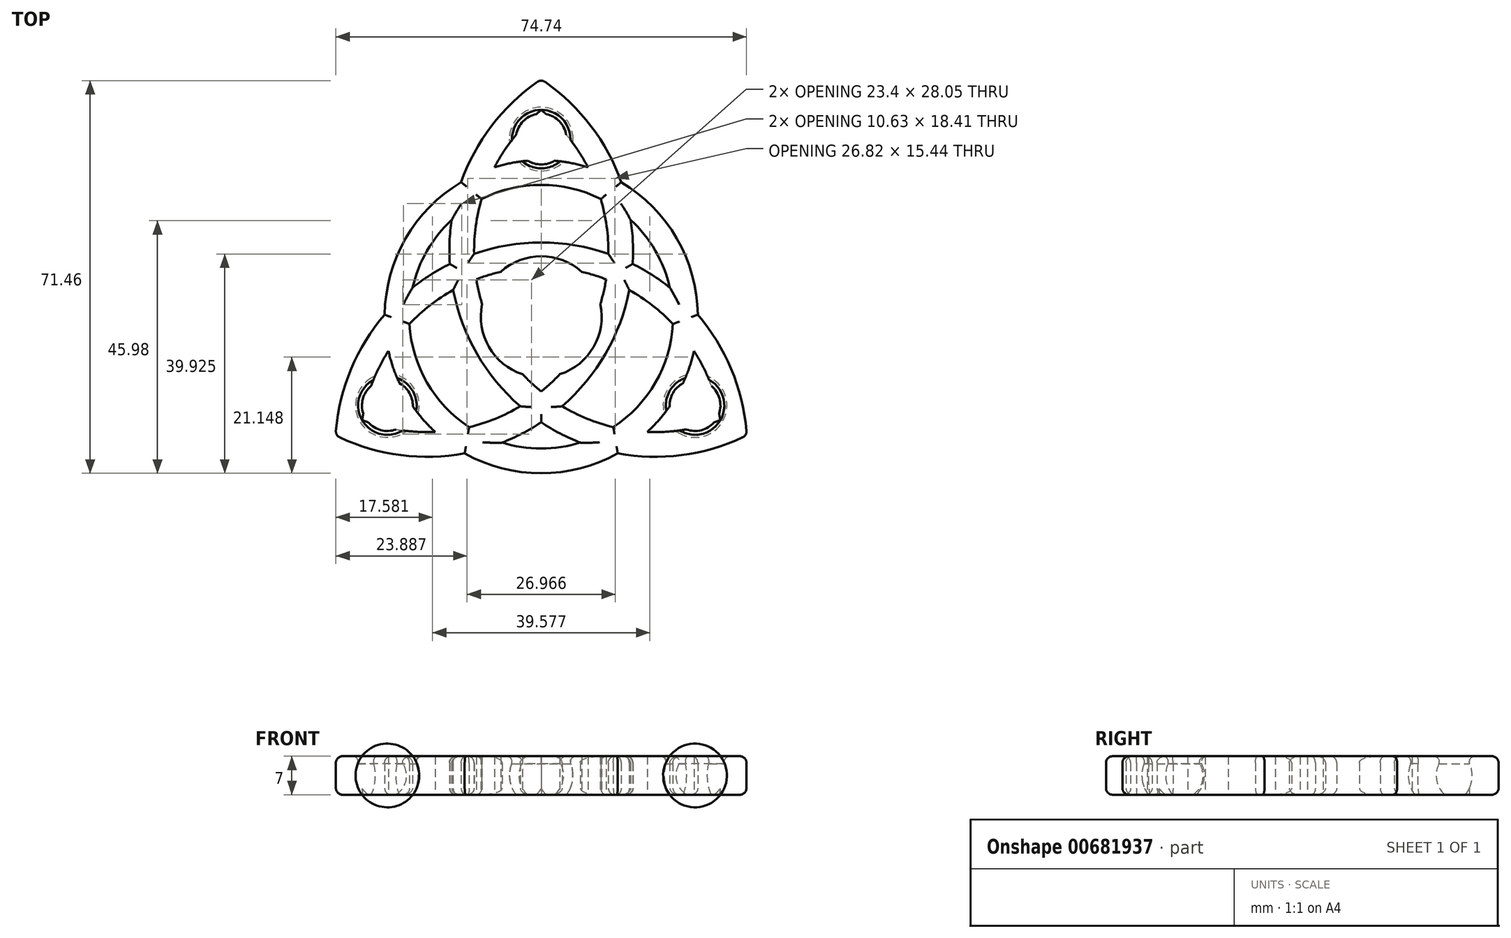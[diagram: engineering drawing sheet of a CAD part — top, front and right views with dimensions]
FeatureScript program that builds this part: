
annotation { "Feature Type Name" : "Feature", "Feature Type Description" : "" }
export const myFeature = defineFeature(function(context is Context, id is Id, definition is map)
    precondition{}
    {
        {
            var Q0;
            Q0=qCreatedBy(makeId("Top.planeOp"),FACE);
            var sketch = newSketch(context, id + "F0", { "sketchPlane" : qUnion([Q0])});
            skLineSegment(sketch, "E0", {"start": v(0, 58.7) * mm, "end": v(0, -66.3) * mm, "construction": true});
            skLineSegment(sketch, "E1", {"start": v(-51.5, -29.73) * mm, "end": v(60.42, 34.88) * mm, "construction": true});
            skLineSegment(sketch, "E2", {"start": v(-60.42, 34.88) * mm, "end": v(51.67, -29.83) * mm, "construction": true});
            skLineSegment(sketch, "E3", {"start": v(-73.13, 34.88) * mm, "end": v(66.87, 34.88) * mm, "construction": true});
            skArc(sketch, "E4", {"start": v(-14.57, 24.5) * mm, "mid": v(-28.35, 2.95) * mm, "end": v(-19.3, -20.97) * mm});
            skArc(sketch, "E5", {"start": v(-16.3, 17.62) * mm, "mid": v(-23.92, -2.01) * mm, "end": v(-13.12, -20.1) * mm});
            skPoint(sketch, "E6", {"position": v(20.78, 12) * mm});
            skArc(sketch, "E7", {"start": v(0, 43.21) * mm, "mid": v(-12.82, 28.64) * mm, "end": v(-16.64, 9.6) * mm});
            skArc(sketch, "E8", {"start": v(0, 37.63) * mm, "mid": v(-9.12, 25.95) * mm, "end": v(-12.21, 11.46) * mm});
            skPoint(sketch, "E9", {"position": v(0, -24) * mm});
            skPoint(sketch, "E10", {"position": v(-20.78, 12) * mm});
            skArc(sketch, "E11", {"start": v(37.42, -21.6) * mm, "mid": v(31.21, -3.22) * mm, "end": v(16.64, 9.6) * mm});
            skArc(sketch, "E12", {"start": v(32.6, -18.82) * mm, "mid": v(27.03, -5.08) * mm, "end": v(16.03, 4.85) * mm});
            skArc(sketch, "E13", {"start": v(-37.42, -21.6) * mm, "mid": v(-18.4, -25.42) * mm, "end": v(0, -19.21) * mm});
            skArc(sketch, "E14", {"start": v(-32.6, -18.82) * mm, "mid": v(-17.91, -20.87) * mm, "end": v(-3.82, -16.3) * mm});
            skArc(sketch, "E15.trimOffspring", {"start": v(8.5, 27.2) * mm, "mid": v(4.8, 32.85) * mm, "end": v(0, 37.63) * mm});
            skArc(sketch, "E16.trimOffspring", {"start": v(14.57, 24.5) * mm, "mid": v(8.8, 35.04) * mm, "end": v(0, 43.21) * mm});
            skArc(sketch, "E17.trimOffspring", {"start": v(12.21, 11.46) * mm, "mid": v(-6.39, 12.95) * mm, "end": v(-23.4, 5.3) * mm});
            skArc(sketch, "E18.trimOffspring", {"start": v(11.8, 6.82) * mm, "mid": v(-7.31, 8.18) * mm, "end": v(-23.96, -1.31) * mm});
            skArc(sketch, "E19.trimOffspring", {"start": v(-11.8, 6.82) * mm, "mid": v(-3.43, -10.42) * mm, "end": v(13.12, -20.1) * mm});
            skArc(sketch, "E20.trimOffspring", {"start": v(-16.03, 4.85) * mm, "mid": v(-8.02, -12) * mm, "end": v(7.12, -22.92) * mm});
            skArc(sketch, "E21.trimOffspring", {"start": v(-7.12, -22.92) * mm, "mid": v(13.7, -19.7) * mm, "end": v(23.96, -1.31) * mm});
            skArc(sketch, "E22.trimOffspring", {"start": v(-13.92, -24.87) * mm, "mid": v(11.62, -26.02) * mm, "end": v(27.8, -6.23) * mm});
            skArc(sketch, "E23.trimOffspring", {"start": v(-27.8, -6.23) * mm, "mid": v(-30.85, -12.28) * mm, "end": v(-32.6, -18.82) * mm});
            skArc(sketch, "E24.trimOffspring", {"start": v(-28.5, 0.37) * mm, "mid": v(-34.74, -9.9) * mm, "end": v(-37.42, -21.6) * mm});
            skArc(sketch, "E25.trimOffspring", {"start": v(13.92, -24.87) * mm, "mid": v(25.94, -25.14) * mm, "end": v(37.42, -21.6) * mm});
            skArc(sketch, "E26.trimOffspring", {"start": v(19.3, -20.97) * mm, "mid": v(26.06, -20.58) * mm, "end": v(32.6, -18.82) * mm});
            skArc(sketch, "E27.trimOffspring", {"start": v(28.5, 0.37) * mm, "mid": v(16.73, 23.07) * mm, "end": v(-8.5, 27.2) * mm});
            skArc(sketch, "E28.trimOffspring", {"start": v(23.4, 5.3) * mm, "mid": v(10.22, 21.72) * mm, "end": v(-10.85, 21.4) * mm});
            skArc(sketch, "E29.trimOffspring", {"start": v(3.82, -16.3) * mm, "mid": v(14.41, -0.94) * mm, "end": v(16.3, 17.62) * mm});
            skArc(sketch, "E30.trimOffspring", {"start": v(0, -13.63) * mm, "mid": v(10.74, 2.24) * mm, "end": v(10.85, 21.4) * mm});
            skSolve(sketch);
        }
        {
            var Q0;
            {var subQ0=sQuery(id+"F0.wireOp",EDGE,"E15.trimOffspring");Q0=makeQuery(id+"F0.imprint","IMPRINT",FACE,{"disambiguationData":[TD([[makeQuery(id+"F0.imprint","IMPRINT",EDGE,{"derivedFrom":subQ0}),-1.0]])]});}
            var Q1;
            {var subQ0=sQuery(id+"F0.wireOp",EDGE,"E27.trimOffspring");var subQ7=sQuery(id+"F0.wireOp",EDGE,"E8");var subQ8=makeQuery(id+"F0.imprint","INTERSECT",VERTEX,{"derivedFrom":[subQ7,subQ0]});Q1=makeQuery(id+"F0.imprint","IMPRINT",FACE,{"disambiguationData":[TD([[makeQuery(id+"F0.imprint","IMPRINT",EDGE,{"disambiguationData":[TD([[subQ8,-1.0]])],"derivedFrom":subQ7}),1.0]])]});}
            var Q2;
            {var subQ0=sQuery(id+"F0.wireOp",EDGE,"E29.trimOffspring");var subQ3=sQuery(id+"F0.wireOp",EDGE,"E19.trimOffspring");var subQ4=makeQuery(id+"F0.imprint","INTERSECT",VERTEX,{"derivedFrom":[subQ3,subQ0]});Q2=makeQuery(id+"F0.imprint","IMPRINT",FACE,{"disambiguationData":[TD([[makeQuery(id+"F0.imprint","IMPRINT",EDGE,{"disambiguationData":[TD([[subQ4,1.0]])],"derivedFrom":subQ3}),1.0]])]});}
            var Q3;
            {var subQ0=sQuery(id+"F0.wireOp",EDGE,"E7");var subQ5=sQuery(id+"F0.wireOp",EDGE,"E4");var subQ9=makeQuery(id+"F0.imprint","INTERSECT",VERTEX,{"derivedFrom":[subQ5,subQ0]});Q3=makeQuery(id+"F0.imprint","IMPRINT",FACE,{"disambiguationData":[TD([[makeQuery(id+"F0.imprint","IMPRINT",EDGE,{"disambiguationData":[TD([[subQ9,-1.0]])],"derivedFrom":subQ5}),1.0]])]});}
            var Q4;
            {var subQ6=sQuery(id+"F0.wireOp",EDGE,"E23.trimOffspring");Q4=makeQuery(id+"F0.imprint","IMPRINT",FACE,{"disambiguationData":[TD([[makeQuery(id+"F0.imprint","IMPRINT",EDGE,{"derivedFrom":subQ6}),-1.0]])]});}
            var Q5;
            {var subQ0=sQuery(id+"F0.wireOp",EDGE,"E21.trimOffspring");var subQ4=sQuery(id+"F0.wireOp",EDGE,"E12");var subQ5=makeQuery(id+"F0.imprint","INTERSECT",VERTEX,{"derivedFrom":[subQ4,subQ0]});Q5=makeQuery(id+"F0.imprint","IMPRINT",FACE,{"disambiguationData":[TD([[makeQuery(id+"F0.imprint","IMPRINT",EDGE,{"disambiguationData":[TD([[subQ5,1.0]])],"derivedFrom":subQ4}),1.0]])]});}
            var Q6;
            {var subQ9=sQuery(id+"F0.wireOp",EDGE,"E25.trimOffspring");Q6=makeQuery(id+"F0.imprint","IMPRINT",FACE,{"disambiguationData":[TD([[makeQuery(id+"F0.imprint","IMPRINT",EDGE,{"derivedFrom":subQ9}),1.0]])]});}
            var Q7;
            {var subQ0=sQuery(id+"F0.wireOp",EDGE,"E17.trimOffspring");var subQ2=sQuery(id+"F0.wireOp",EDGE,"E5");var subQ3=makeQuery(id+"F0.imprint","INTERSECT",VERTEX,{"derivedFrom":[subQ2,subQ0]});Q7=makeQuery(id+"F0.imprint","IMPRINT",FACE,{"disambiguationData":[TD([[makeQuery(id+"F0.imprint","IMPRINT",EDGE,{"disambiguationData":[TD([[subQ3,-1.0]])],"derivedFrom":subQ2}),1.0]])]});}
            var Q8;
            {var subQ1=sQuery(id+"F0.wireOp",EDGE,"E19.trimOffspring");var subQ5=sQuery(id+"F0.wireOp",EDGE,"E18.trimOffspring");var subQ6=makeQuery(id+"F0.imprint","INTERSECT",VERTEX,{"derivedFrom":[subQ5,subQ1]});Q8=makeQuery(id+"F0.imprint","IMPRINT",FACE,{"disambiguationData":[TD([[makeQuery(id+"F0.imprint","IMPRINT",EDGE,{"disambiguationData":[TD([[subQ6,-1.0]])],"derivedFrom":subQ5}),1.0]])]});}
            extrude(context, id + "F1", {"entities" : qUnion([Q0, Q1, Q2, Q3, Q4, Q5, Q6, Q7, Q8]), "depth" : 7 * mm, "offsetDistance" : 25 * mm});
        }
        {
            var Q0;
            Q0=qCreatedBy(makeId("Top.planeOp"),FACE);
            var sketch = newSketch(context, id + "F2", { "sketchPlane" : qUnion([Q0])});
            skCircle(sketch, "E31", {"center": v(0, 0) * mm, "radius": 11 * mm});
            skPoint(sketch, "E32", {"position": v(0, 32.33) * mm});
            skPoint(sketch, "E33.0", {"position": v(0, 37.63) * mm});
            skPoint(sketch, "E34.0", {"position": v(0, 28.5) * mm});
            skPoint(sketch, "E35.0", {"position": v(24.68, -14.25) * mm});
            skPoint(sketch, "E36.0", {"position": v(32.6, -18.82) * mm});
            skPoint(sketch, "E37.0", {"position": v(-32.6, -18.82) * mm});
            skPoint(sketch, "E38.0", {"position": v(-24.68, -14.25) * mm});
            skCircle(sketch, "E39", {"center": v(0, 32.33) * mm, "radius": 5.8 * mm});
            skLineSegment(sketch, "E40", {"start": v(-46.33, -26.75) * mm, "end": v(57.59, 33.25) * mm, "construction": true});
            skLineSegment(sketch, "E41", {"start": v(-57.33, 33.1) * mm, "end": v(46.6, -26.9) * mm, "construction": true});
            skCircle(sketch, "E42.MirrorC", {"center": v(-28, -16.17) * mm, "radius": 5.8 * mm});
            skCircle(sketch, "E43.MirrorC", {"center": v(28, -16.17) * mm, "radius": 5.8 * mm});
            skLineSegment(sketch, "E44", {"start": v(-5.8, 32.33) * mm, "end": v(5.8, 32.33) * mm});
            skLineSegment(sketch, "E45.MirrorCS", {"start": v(-30.9, -11.14) * mm, "end": v(-25.1, -21.19) * mm});
            skLineSegment(sketch, "E46.MirrorCS", {"start": v(25.1, -21.19) * mm, "end": v(30.9, -11.14) * mm});
            skSolve(sketch);
        }
        {
            var Q0;
            Q0=makeQuery(id+"F2.imprint","IMPRINT",FACE,{"disambiguationData":[TD([[makeQuery(id+"F2.imprint","IMPRINT",EDGE,{"derivedFrom":sQuery(id+"F2.wireOp",EDGE,"E31")}),1.0]])]});
            extrude(context, id + "F3", {"entities" : qUnion([Q0]), "operationType" : NewBodyOperationType.REMOVE, "depth" : 7 * mm, "offsetDistance" : 25 * mm});
        }
        {
            var Q0;
            Q0=qCreatedBy(makeId("Top.planeOp"),FACE);
            cPlane(context, id + "F4", {"entities" : qUnion([Q0]), "cplaneType" : CPlaneType.OFFSET, "offset" : 3.5 * mm, "width" : 150 * mm, "height" : 150 * mm});
        }
        {
            var Q0;
            Q0=qCreatedBy(id+"F4.planeOp",FACE);
            var sketch = newSketch(context, id + "F5", { "sketchPlane" : qUnion([Q0])});
            skLineSegment(sketch, "E47.0", {"start": v(-5.8, 32.33) * mm, "end": v(5.8, 32.33) * mm});
            skCircle(sketch, "E48.0", {"center": v(0, 32.33) * mm, "radius": 5.8 * mm});
            skPoint(sketch, "E49.0", {"position": v(28, -16.17) * mm});
            skCircle(sketch, "E50.0", {"center": v(28, -16.17) * mm, "radius": 5.8 * mm});
            skLineSegment(sketch, "E51.0", {"start": v(25.1, -21.19) * mm, "end": v(30.9, -11.14) * mm});
            skCircle(sketch, "E52.0", {"center": v(-28, -16.17) * mm, "radius": 5.8 * mm});
            skLineSegment(sketch, "E53.0", {"start": v(-30.9, -11.14) * mm, "end": v(-25.1, -21.19) * mm});
            skSolve(sketch);
        }
        {
            var Q0;
            {var subQ0=sQuery(id+"F5.wireOp",EDGE,"E47.0");Q0=makeQuery(id+"F5.imprint","IMPRINT",FACE,{"disambiguationData":[TD([[makeQuery(id+"F5.imprint","IMPRINT",EDGE,{"derivedFrom":subQ0}),1.0]])]});}
            var Q1;
            Q1=sQuery(id+"F5.wireOp",EDGE,"E47.0");
            revolve(context, id + "F6", {"operationType" : NewBodyOperationType.REMOVE, "entities" : qUnion([Q0]), "axis" : qUnion([Q1]), "revolveType" : RevolveType.FULL, "oppositeDirection" : true});
        }
        {
            var Q0;
            {var subQ0=sQuery(id+"F5.wireOp",EDGE,"E53.0");Q0=makeQuery(id+"F5.imprint","IMPRINT",FACE,{"disambiguationData":[TD([[makeQuery(id+"F5.imprint","IMPRINT",EDGE,{"derivedFrom":subQ0}),-1.0]])]});}
            var Q1;
            Q1=sQuery(id+"F5.wireOp",EDGE,"E53.0");
            revolve(context, id + "F7", {"operationType" : NewBodyOperationType.REMOVE, "entities" : qUnion([Q0]), "axis" : qUnion([Q1]), "revolveType" : RevolveType.FULL, "oppositeDirection" : true});
        }
        {
            var Q0;
            {var subQ0=sQuery(id+"F5.wireOp",EDGE,"E51.0");Q0=makeQuery(id+"F5.imprint","IMPRINT",FACE,{"disambiguationData":[TD([[makeQuery(id+"F5.imprint","IMPRINT",EDGE,{"derivedFrom":subQ0}),-1.0]])]});}
            var Q1;
            Q1=sQuery(id+"F5.wireOp",EDGE,"E51.0");
            revolve(context, id + "F8", {"operationType" : NewBodyOperationType.REMOVE, "entities" : qUnion([Q0]), "axis" : qUnion([Q1]), "revolveType" : RevolveType.FULL, "oppositeDirection" : true});
        }
        {
            var Q0;
            {var subQ0=sQuery(id+"F0.wireOp",EDGE,"E7");Q0=makeQuery(id+"F1.opExtrude","CAP_EDGE",EDGE,{"disambiguationData":[OSD([subQ0]),TDD([makeQuery(id+"F0.imprint","IMPRINT",EDGE,{"disambiguationData":[TD([[makeQuery(id+"F0.imprint","INTERSECT",VERTEX,{"derivedFrom":[sQuery(id+"F0.wireOp",EDGE,"E4"),subQ0]}),1.0]])],"derivedFrom":subQ0})])],"isStart":false});}
            var Q1;
            Q1=makeQuery(id+"F1.opExtrude","CAP_EDGE",EDGE,{"disambiguationData":[OSD([sQuery(id+"F0.wireOp",EDGE,"E16.trimOffspring")])],"isStart":false});
            var Q2;
            Q2=makeQuery(id+"F1.opExtrude","SWEPT_EDGE",EDGE,{"disambiguationData":[OSD([sQuery(id+"F0.wireOp",EDGE,"E7"),sQuery(id+"F0.wireOp",EDGE,"E16.trimOffspring")])]});
            var Q3;
            {var subQ0=sQuery(id+"F0.wireOp",EDGE,"E4");Q3=makeQuery(id+"F1.opExtrude","CAP_EDGE",EDGE,{"disambiguationData":[OSD([subQ0]),TDD([makeQuery(id+"F0.imprint","IMPRINT",EDGE,{"disambiguationData":[TD([[makeQuery(id+"F0.imprint","INTERSECT",VERTEX,{"derivedFrom":[subQ0,sQuery(id+"F0.wireOp",EDGE,"E7")]}),-1.0]])],"derivedFrom":subQ0})])],"isStart":false});}
            var Q4;
            {var subQ0=sQuery(id+"F0.wireOp",EDGE,"E7");Q4=makeQuery(id+"F1.opExtrude","CAP_EDGE",EDGE,{"disambiguationData":[OSD([subQ0]),TDD([makeQuery(id+"F0.imprint","IMPRINT",EDGE,{"disambiguationData":[TD([[makeQuery(id+"F0.imprint","INTERSECT",VERTEX,{"derivedFrom":[sQuery(id+"F0.wireOp",EDGE,"E5"),subQ0]}),-1.0]])],"derivedFrom":subQ0})])],"isStart":false});}
            var Q5;
            {var subQ0=sQuery(id+"F0.wireOp",EDGE,"E5");Q5=makeQuery(id+"F1.opExtrude","CAP_EDGE",EDGE,{"disambiguationData":[OSD([subQ0]),TDD([makeQuery(id+"F0.imprint","IMPRINT",EDGE,{"disambiguationData":[TD([[makeQuery(id+"F0.imprint","INTERSECT",VERTEX,{"derivedFrom":[subQ0,sQuery(id+"F0.wireOp",EDGE,"E7")]}),-1.0]])],"derivedFrom":subQ0})])],"isStart":false});}
            var Q6;
            {var subQ0=sQuery(id+"F0.wireOp",EDGE,"E17.trimOffspring");Q6=makeQuery(id+"F1.opExtrude","CAP_EDGE",EDGE,{"disambiguationData":[OSD([subQ0]),TDD([makeQuery(id+"F0.imprint","IMPRINT",EDGE,{"disambiguationData":[TD([[makeQuery(id+"F0.imprint","INTERSECT",VERTEX,{"derivedFrom":[sQuery(id+"F0.wireOp",EDGE,"E7"),subQ0]}),-1.0]])],"derivedFrom":subQ0})])],"isStart":false});}
            var Q7;
            {var subQ0=sQuery(id+"F0.wireOp",EDGE,"E17.trimOffspring");Q7=makeQuery(id+"F1.opExtrude","CAP_EDGE",EDGE,{"disambiguationData":[OSD([subQ0]),TDD([makeQuery(id+"F0.imprint","IMPRINT",EDGE,{"disambiguationData":[TD([[makeQuery(id+"F0.imprint","INTERSECT",VERTEX,{"derivedFrom":[sQuery(id+"F0.wireOp",EDGE,"E8"),subQ0]}),1.0]])],"derivedFrom":subQ0})])],"isStart":false});}
            var Q8;
            {var subQ0=sQuery(id+"F0.wireOp",EDGE,"E8");Q8=makeQuery(id+"F1.opExtrude","CAP_EDGE",EDGE,{"disambiguationData":[OSD([subQ0]),TDD([makeQuery(id+"F0.imprint","IMPRINT",EDGE,{"disambiguationData":[TD([[makeQuery(id+"F0.imprint","INTERSECT",VERTEX,{"derivedFrom":[subQ0,sQuery(id+"F0.wireOp",EDGE,"E17.trimOffspring")]}),1.0]])],"derivedFrom":subQ0})])],"isStart":false});}
            var Q9;
            {var subQ0=sQuery(id+"F0.wireOp",EDGE,"E28.trimOffspring");Q9=makeQuery(id+"F1.opExtrude","CAP_EDGE",EDGE,{"disambiguationData":[OSD([subQ0]),TDD([makeQuery(id+"F0.imprint","IMPRINT",EDGE,{"disambiguationData":[TD([[makeQuery(id+"F0.imprint","INTERSECT",VERTEX,{"derivedFrom":[sQuery(id+"F0.wireOp",EDGE,"E8"),subQ0]}),1.0]])],"derivedFrom":subQ0})])],"isStart":false});}
            var Q10;
            {var subQ0=sQuery(id+"F0.wireOp",EDGE,"E30.trimOffspring");Q10=makeQuery(id+"F1.opExtrude","CAP_EDGE",EDGE,{"disambiguationData":[OSD([subQ0]),TDD([makeQuery(id+"F0.imprint","IMPRINT",EDGE,{"disambiguationData":[TD([[makeQuery(id+"F0.imprint","INTERSECT",VERTEX,{"derivedFrom":[sQuery(id+"F0.wireOp",EDGE,"E17.trimOffspring"),subQ0]}),-1.0]])],"derivedFrom":subQ0})])],"isStart":false});}
            var Q11;
            {var subQ0=sQuery(id+"F0.wireOp",EDGE,"E29.trimOffspring");Q11=makeQuery(id+"F1.opExtrude","CAP_EDGE",EDGE,{"disambiguationData":[OSD([subQ0]),TDD([makeQuery(id+"F0.imprint","IMPRINT",EDGE,{"disambiguationData":[TD([[makeQuery(id+"F0.imprint","INTERSECT",VERTEX,{"derivedFrom":[sQuery(id+"F0.wireOp",EDGE,"E11"),subQ0]}),-1.0]])],"derivedFrom":subQ0})])],"isStart":false});}
            var Q12;
            {var subQ0=sQuery(id+"F0.wireOp",EDGE,"E28.trimOffspring");Q12=makeQuery(id+"F1.opExtrude","CAP_EDGE",EDGE,{"disambiguationData":[OSD([subQ0]),TDD([makeQuery(id+"F0.imprint","IMPRINT",EDGE,{"disambiguationData":[TD([[makeQuery(id+"F0.imprint","INTERSECT",VERTEX,{"derivedFrom":[sQuery(id+"F0.wireOp",EDGE,"E11"),subQ0]}),-1.0]])],"derivedFrom":subQ0})])],"isStart":false});}
            var Q13;
            {var subQ0=sQuery(id+"F0.wireOp",EDGE,"E11");Q13=makeQuery(id+"F1.opExtrude","CAP_EDGE",EDGE,{"disambiguationData":[OSD([subQ0]),TDD([makeQuery(id+"F0.imprint","IMPRINT",EDGE,{"disambiguationData":[TD([[makeQuery(id+"F0.imprint","INTERSECT",VERTEX,{"derivedFrom":[subQ0,sQuery(id+"F0.wireOp",EDGE,"E29.trimOffspring")]}),1.0]])],"derivedFrom":subQ0})])],"isStart":false});}
            var Q14;
            {var subQ0=sQuery(id+"F0.wireOp",EDGE,"E27.trimOffspring");Q14=makeQuery(id+"F1.opExtrude","CAP_EDGE",EDGE,{"disambiguationData":[OSD([subQ0]),TDD([makeQuery(id+"F0.imprint","IMPRINT",EDGE,{"disambiguationData":[TD([[makeQuery(id+"F0.imprint","INTERSECT",VERTEX,{"derivedFrom":[sQuery(id+"F0.wireOp",EDGE,"E16.trimOffspring"),subQ0]}),1.0]])],"derivedFrom":subQ0})])],"isStart":false});}
            var Q15;
            {var subQ0=sQuery(id+"F0.wireOp",EDGE,"E11");Q15=makeQuery(id+"F1.opExtrude","CAP_EDGE",EDGE,{"disambiguationData":[OSD([subQ0]),TDD([makeQuery(id+"F0.imprint","IMPRINT",EDGE,{"disambiguationData":[TD([[makeQuery(id+"F0.imprint","INTERSECT",VERTEX,{"derivedFrom":[subQ0,sQuery(id+"F0.wireOp",EDGE,"E25.trimOffspring")]}),-1.0]])],"derivedFrom":subQ0})])],"isStart":false});}
            var Q16;
            {var subQ0=sQuery(id+"F0.wireOp",EDGE,"E21.trimOffspring");Q16=makeQuery(id+"F1.opExtrude","CAP_EDGE",EDGE,{"disambiguationData":[OSD([subQ0]),TDD([makeQuery(id+"F0.imprint","IMPRINT",EDGE,{"disambiguationData":[TD([[makeQuery(id+"F0.imprint","INTERSECT",VERTEX,{"derivedFrom":[sQuery(id+"F0.wireOp",EDGE,"E19.trimOffspring"),subQ0]}),-1.0]])],"derivedFrom":subQ0})])],"isStart":false});}
            var Q17;
            {var subQ0=sQuery(id+"F0.wireOp",EDGE,"E29.trimOffspring");Q17=makeQuery(id+"F1.opExtrude","CAP_EDGE",EDGE,{"disambiguationData":[OSD([subQ0]),TDD([makeQuery(id+"F0.imprint","IMPRINT",EDGE,{"disambiguationData":[TD([[makeQuery(id+"F0.imprint","INTERSECT",VERTEX,{"derivedFrom":[sQuery(id+"F0.wireOp",EDGE,"E12"),subQ0]}),1.0]])],"derivedFrom":subQ0})])],"isStart":false});}
            var Q18;
            {var subQ0=sQuery(id+"F0.wireOp",EDGE,"E20.trimOffspring");Q18=makeQuery(id+"F1.opExtrude","CAP_EDGE",EDGE,{"disambiguationData":[OSD([subQ0]),TDD([makeQuery(id+"F0.imprint","IMPRINT",EDGE,{"disambiguationData":[TD([[makeQuery(id+"F0.imprint","INTERSECT",VERTEX,{"derivedFrom":[sQuery(id+"F0.wireOp",EDGE,"E14"),subQ0]}),1.0]])],"derivedFrom":subQ0})])],"isStart":false});}
            var Q19;
            {var subQ0=sQuery(id+"F0.wireOp",EDGE,"E14");Q19=makeQuery(id+"F1.opExtrude","CAP_EDGE",EDGE,{"disambiguationData":[OSD([subQ0]),TDD([makeQuery(id+"F0.imprint","IMPRINT",EDGE,{"disambiguationData":[TD([[makeQuery(id+"F0.imprint","INTERSECT",VERTEX,{"derivedFrom":[sQuery(id+"F0.wireOp",EDGE,"E5"),subQ0]}),-1.0]])],"derivedFrom":subQ0})])],"isStart":false});}
            var Q20;
            {var subQ0=sQuery(id+"F0.wireOp",EDGE,"E5");Q20=makeQuery(id+"F1.opExtrude","CAP_EDGE",EDGE,{"disambiguationData":[OSD([subQ0]),TDD([makeQuery(id+"F0.imprint","IMPRINT",EDGE,{"disambiguationData":[TD([[makeQuery(id+"F0.imprint","INTERSECT",VERTEX,{"derivedFrom":[subQ0,sQuery(id+"F0.wireOp",EDGE,"E14")]}),1.0]])],"derivedFrom":subQ0})])],"isStart":false});}
            var Q21;
            {var subQ0=sQuery(id+"F0.wireOp",EDGE,"E18.trimOffspring");Q21=makeQuery(id+"F1.opExtrude","CAP_EDGE",EDGE,{"disambiguationData":[OSD([subQ0]),TDD([makeQuery(id+"F0.imprint","IMPRINT",EDGE,{"disambiguationData":[TD([[makeQuery(id+"F0.imprint","INTERSECT",VERTEX,{"derivedFrom":[sQuery(id+"F0.wireOp",EDGE,"E5"),subQ0]}),1.0]])],"derivedFrom":subQ0})])],"isStart":false});}
            var Q22;
            Q22=makeQuery(id+"F1.opExtrude","CAP_EDGE",EDGE,{"disambiguationData":[OSD([sQuery(id+"F0.wireOp",EDGE,"E25.trimOffspring")])],"isStart":false});
            var Q23;
            {var subQ0=sQuery(id+"F0.wireOp",EDGE,"E22.trimOffspring");Q23=makeQuery(id+"F1.opExtrude","CAP_EDGE",EDGE,{"disambiguationData":[OSD([subQ0]),TDD([makeQuery(id+"F0.imprint","IMPRINT",EDGE,{"disambiguationData":[TD([[makeQuery(id+"F0.imprint","INTERSECT",VERTEX,{"derivedFrom":[sQuery(id+"F0.wireOp",EDGE,"E13"),subQ0]}),-1.0]])],"derivedFrom":subQ0})])],"isStart":false});}
            var Q24;
            Q24=makeQuery(id+"F1.opExtrude","SWEPT_EDGE",EDGE,{"disambiguationData":[OSD([sQuery(id+"F0.wireOp",EDGE,"E11"),sQuery(id+"F0.wireOp",EDGE,"E25.trimOffspring")])]});
            var Q25;
            Q25=makeQuery(id+"F1.opExtrude","CAP_EDGE",EDGE,{"disambiguationData":[OSD([sQuery(id+"F0.wireOp",EDGE,"E24.trimOffspring")])],"isStart":false});
            var Q26;
            {var subQ0=sQuery(id+"F0.wireOp",EDGE,"E13");Q26=makeQuery(id+"F1.opExtrude","CAP_EDGE",EDGE,{"disambiguationData":[OSD([subQ0]),TDD([makeQuery(id+"F0.imprint","IMPRINT",EDGE,{"disambiguationData":[TD([[makeQuery(id+"F0.imprint","INTERSECT",VERTEX,{"derivedFrom":[subQ0,sQuery(id+"F0.wireOp",EDGE,"E24.trimOffspring")]}),-1.0]])],"derivedFrom":subQ0})])],"isStart":false});}
            var Q27;
            Q27=makeQuery(id+"F1.opExtrude","SWEPT_EDGE",EDGE,{"disambiguationData":[OSD([sQuery(id+"F0.wireOp",EDGE,"E13"),sQuery(id+"F0.wireOp",EDGE,"E24.trimOffspring")])]});
            var Q28;
            Q28=makeQuery(id+"F1.opExtrude","CAP_EDGE",EDGE,{"disambiguationData":[OSD([sQuery(id+"F0.wireOp",EDGE,"E24.trimOffspring")])],"isStart":true});
            var Q29;
            {var subQ0=sQuery(id+"F0.wireOp",EDGE,"E5");Q29=makeQuery(id+"F1.opExtrude","CAP_EDGE",EDGE,{"disambiguationData":[OSD([subQ0]),TDD([makeQuery(id+"F0.imprint","IMPRINT",EDGE,{"disambiguationData":[TD([[makeQuery(id+"F0.imprint","INTERSECT",VERTEX,{"derivedFrom":[subQ0,sQuery(id+"F0.wireOp",EDGE,"E14")]}),1.0]])],"derivedFrom":subQ0})])],"isStart":true});}
            var Q30;
            {var subQ0=sQuery(id+"F0.wireOp",EDGE,"E18.trimOffspring");Q30=makeQuery(id+"F1.opExtrude","CAP_EDGE",EDGE,{"disambiguationData":[OSD([subQ0]),TDD([makeQuery(id+"F0.imprint","IMPRINT",EDGE,{"disambiguationData":[TD([[makeQuery(id+"F0.imprint","INTERSECT",VERTEX,{"derivedFrom":[sQuery(id+"F0.wireOp",EDGE,"E5"),subQ0]}),1.0]])],"derivedFrom":subQ0})])],"isStart":true});}
            var Q31;
            {var subQ0=sQuery(id+"F0.wireOp",EDGE,"E20.trimOffspring");Q31=makeQuery(id+"F1.opExtrude","CAP_EDGE",EDGE,{"disambiguationData":[OSD([subQ0]),TDD([makeQuery(id+"F0.imprint","IMPRINT",EDGE,{"disambiguationData":[TD([[makeQuery(id+"F0.imprint","INTERSECT",VERTEX,{"derivedFrom":[sQuery(id+"F0.wireOp",EDGE,"E14"),subQ0]}),1.0]])],"derivedFrom":subQ0})])],"isStart":true});}
            var Q32;
            {var subQ0=sQuery(id+"F0.wireOp",EDGE,"E5");Q32=makeQuery(id+"F1.opExtrude","CAP_EDGE",EDGE,{"disambiguationData":[OSD([subQ0]),TDD([makeQuery(id+"F0.imprint","IMPRINT",EDGE,{"disambiguationData":[TD([[makeQuery(id+"F0.imprint","INTERSECT",VERTEX,{"derivedFrom":[subQ0,sQuery(id+"F0.wireOp",EDGE,"E7")]}),-1.0]])],"derivedFrom":subQ0})])],"isStart":true});}
            var Q33;
            {var subQ0=sQuery(id+"F0.wireOp",EDGE,"E17.trimOffspring");Q33=makeQuery(id+"F1.opExtrude","CAP_EDGE",EDGE,{"disambiguationData":[OSD([subQ0]),TDD([makeQuery(id+"F0.imprint","IMPRINT",EDGE,{"disambiguationData":[TD([[makeQuery(id+"F0.imprint","INTERSECT",VERTEX,{"derivedFrom":[sQuery(id+"F0.wireOp",EDGE,"E7"),subQ0]}),-1.0]])],"derivedFrom":subQ0})])],"isStart":true});}
            var Q34;
            {var subQ0=sQuery(id+"F0.wireOp",EDGE,"E4");Q34=makeQuery(id+"F1.opExtrude","CAP_EDGE",EDGE,{"disambiguationData":[OSD([subQ0]),TDD([makeQuery(id+"F0.imprint","IMPRINT",EDGE,{"disambiguationData":[TD([[makeQuery(id+"F0.imprint","INTERSECT",VERTEX,{"derivedFrom":[subQ0,sQuery(id+"F0.wireOp",EDGE,"E7")]}),-1.0]])],"derivedFrom":subQ0})])],"isStart":true});}
            var Q35;
            {var subQ0=sQuery(id+"F0.wireOp",EDGE,"E7");Q35=makeQuery(id+"F1.opExtrude","CAP_EDGE",EDGE,{"disambiguationData":[OSD([subQ0]),TDD([makeQuery(id+"F0.imprint","IMPRINT",EDGE,{"disambiguationData":[TD([[makeQuery(id+"F0.imprint","INTERSECT",VERTEX,{"derivedFrom":[sQuery(id+"F0.wireOp",EDGE,"E4"),subQ0]}),1.0]])],"derivedFrom":subQ0})])],"isStart":true});}
            var Q36;
            {var subQ0=sQuery(id+"F0.wireOp",EDGE,"E7");Q36=makeQuery(id+"F1.opExtrude","CAP_EDGE",EDGE,{"disambiguationData":[OSD([subQ0]),TDD([makeQuery(id+"F0.imprint","IMPRINT",EDGE,{"disambiguationData":[TD([[makeQuery(id+"F0.imprint","INTERSECT",VERTEX,{"derivedFrom":[sQuery(id+"F0.wireOp",EDGE,"E5"),subQ0]}),-1.0]])],"derivedFrom":subQ0})])],"isStart":true});}
            var Q37;
            {var subQ0=sQuery(id+"F0.wireOp",EDGE,"E17.trimOffspring");Q37=makeQuery(id+"F1.opExtrude","CAP_EDGE",EDGE,{"disambiguationData":[OSD([subQ0]),TDD([makeQuery(id+"F0.imprint","IMPRINT",EDGE,{"disambiguationData":[TD([[makeQuery(id+"F0.imprint","INTERSECT",VERTEX,{"derivedFrom":[sQuery(id+"F0.wireOp",EDGE,"E8"),subQ0]}),1.0]])],"derivedFrom":subQ0})])],"isStart":true});}
            var Q38;
            {var subQ0=sQuery(id+"F0.wireOp",EDGE,"E14");Q38=makeQuery(id+"F1.opExtrude","CAP_EDGE",EDGE,{"disambiguationData":[OSD([subQ0]),TDD([makeQuery(id+"F0.imprint","IMPRINT",EDGE,{"disambiguationData":[TD([[makeQuery(id+"F0.imprint","INTERSECT",VERTEX,{"derivedFrom":[sQuery(id+"F0.wireOp",EDGE,"E5"),subQ0]}),-1.0]])],"derivedFrom":subQ0})])],"isStart":true});}
            var Q39;
            {var subQ0=sQuery(id+"F0.wireOp",EDGE,"E13");Q39=makeQuery(id+"F1.opExtrude","CAP_EDGE",EDGE,{"disambiguationData":[OSD([subQ0]),TDD([makeQuery(id+"F0.imprint","IMPRINT",EDGE,{"disambiguationData":[TD([[makeQuery(id+"F0.imprint","INTERSECT",VERTEX,{"derivedFrom":[subQ0,sQuery(id+"F0.wireOp",EDGE,"E20.trimOffspring")]}),1.0]])],"derivedFrom":subQ0})])],"isStart":true});}
            var Q40;
            {var subQ0=sQuery(id+"F0.wireOp",EDGE,"E21.trimOffspring");Q40=makeQuery(id+"F1.opExtrude","CAP_EDGE",EDGE,{"disambiguationData":[OSD([subQ0]),TDD([makeQuery(id+"F0.imprint","IMPRINT",EDGE,{"disambiguationData":[TD([[makeQuery(id+"F0.imprint","INTERSECT",VERTEX,{"derivedFrom":[sQuery(id+"F0.wireOp",EDGE,"E20.trimOffspring"),subQ0]}),1.0]])],"derivedFrom":subQ0})])],"isStart":true});}
            var Q41;
            {var subQ0=sQuery(id+"F0.wireOp",EDGE,"E20.trimOffspring");Q41=makeQuery(id+"F1.opExtrude","CAP_EDGE",EDGE,{"disambiguationData":[OSD([subQ0]),TDD([makeQuery(id+"F0.imprint","IMPRINT",EDGE,{"disambiguationData":[TD([[makeQuery(id+"F0.imprint","INTERSECT",VERTEX,{"derivedFrom":[sQuery(id+"F0.wireOp",EDGE,"E13"),subQ0]}),-1.0]])],"derivedFrom":subQ0})])],"isStart":true});}
            var Q42;
            {var subQ0=sQuery(id+"F0.wireOp",EDGE,"E13");Q42=makeQuery(id+"F1.opExtrude","CAP_EDGE",EDGE,{"disambiguationData":[OSD([subQ0]),TDD([makeQuery(id+"F0.imprint","IMPRINT",EDGE,{"disambiguationData":[TD([[makeQuery(id+"F0.imprint","INTERSECT",VERTEX,{"derivedFrom":[subQ0,sQuery(id+"F0.wireOp",EDGE,"E24.trimOffspring")]}),-1.0]])],"derivedFrom":subQ0})])],"isStart":true});}
            var Q43;
            {var subQ0=sQuery(id+"F0.wireOp",EDGE,"E22.trimOffspring");Q43=makeQuery(id+"F1.opExtrude","CAP_EDGE",EDGE,{"disambiguationData":[OSD([subQ0]),TDD([makeQuery(id+"F0.imprint","IMPRINT",EDGE,{"disambiguationData":[TD([[makeQuery(id+"F0.imprint","INTERSECT",VERTEX,{"derivedFrom":[sQuery(id+"F0.wireOp",EDGE,"E13"),subQ0]}),-1.0]])],"derivedFrom":subQ0})])],"isStart":true});}
            var Q44;
            {var subQ0=sQuery(id+"F0.wireOp",EDGE,"E29.trimOffspring");Q44=makeQuery(id+"F1.opExtrude","CAP_EDGE",EDGE,{"disambiguationData":[OSD([subQ0]),TDD([makeQuery(id+"F0.imprint","IMPRINT",EDGE,{"disambiguationData":[TD([[makeQuery(id+"F0.imprint","INTERSECT",VERTEX,{"derivedFrom":[sQuery(id+"F0.wireOp",EDGE,"E12"),subQ0]}),1.0]])],"derivedFrom":subQ0})])],"isStart":true});}
            var Q45;
            {var subQ0=sQuery(id+"F0.wireOp",EDGE,"E19.trimOffspring");Q45=makeQuery(id+"F1.opExtrude","CAP_EDGE",EDGE,{"disambiguationData":[OSD([subQ0]),TDD([makeQuery(id+"F0.imprint","IMPRINT",EDGE,{"disambiguationData":[TD([[makeQuery(id+"F0.imprint","INTERSECT",VERTEX,{"derivedFrom":[subQ0,sQuery(id+"F0.wireOp",EDGE,"E21.trimOffspring")]}),1.0]])],"derivedFrom":subQ0})])],"isStart":true});}
            var Q46;
            {var subQ0=sQuery(id+"F0.wireOp",EDGE,"E8");Q46=makeQuery(id+"F1.opExtrude","CAP_EDGE",EDGE,{"disambiguationData":[OSD([subQ0]),TDD([makeQuery(id+"F0.imprint","IMPRINT",EDGE,{"disambiguationData":[TD([[makeQuery(id+"F0.imprint","INTERSECT",VERTEX,{"derivedFrom":[subQ0,sQuery(id+"F0.wireOp",EDGE,"E17.trimOffspring")]}),1.0]])],"derivedFrom":subQ0})])],"isStart":true});}
            var Q47;
            {var subQ0=sQuery(id+"F0.wireOp",EDGE,"E28.trimOffspring");Q47=makeQuery(id+"F1.opExtrude","CAP_EDGE",EDGE,{"disambiguationData":[OSD([subQ0]),TDD([makeQuery(id+"F0.imprint","IMPRINT",EDGE,{"disambiguationData":[TD([[makeQuery(id+"F0.imprint","INTERSECT",VERTEX,{"derivedFrom":[sQuery(id+"F0.wireOp",EDGE,"E8"),subQ0]}),1.0]])],"derivedFrom":subQ0})])],"isStart":true});}
            var Q48;
            {var subQ0=sQuery(id+"F0.wireOp",EDGE,"E21.trimOffspring");Q48=makeQuery(id+"F1.opExtrude","CAP_EDGE",EDGE,{"disambiguationData":[OSD([subQ0]),TDD([makeQuery(id+"F0.imprint","IMPRINT",EDGE,{"disambiguationData":[TD([[makeQuery(id+"F0.imprint","INTERSECT",VERTEX,{"derivedFrom":[sQuery(id+"F0.wireOp",EDGE,"E19.trimOffspring"),subQ0]}),-1.0]])],"derivedFrom":subQ0})])],"isStart":true});}
            var Q49;
            Q49=makeQuery(id+"F1.opExtrude","CAP_EDGE",EDGE,{"disambiguationData":[OSD([sQuery(id+"F0.wireOp",EDGE,"E16.trimOffspring")])],"isStart":true});
            var Q50;
            {var subQ0=sQuery(id+"F0.wireOp",EDGE,"E27.trimOffspring");Q50=makeQuery(id+"F1.opExtrude","CAP_EDGE",EDGE,{"disambiguationData":[OSD([subQ0]),TDD([makeQuery(id+"F0.imprint","IMPRINT",EDGE,{"disambiguationData":[TD([[makeQuery(id+"F0.imprint","INTERSECT",VERTEX,{"derivedFrom":[sQuery(id+"F0.wireOp",EDGE,"E16.trimOffspring"),subQ0]}),1.0]])],"derivedFrom":subQ0})])],"isStart":true});}
            var Q51;
            {var subQ0=sQuery(id+"F0.wireOp",EDGE,"E28.trimOffspring");Q51=makeQuery(id+"F1.opExtrude","CAP_EDGE",EDGE,{"disambiguationData":[OSD([subQ0]),TDD([makeQuery(id+"F0.imprint","IMPRINT",EDGE,{"disambiguationData":[TD([[makeQuery(id+"F0.imprint","INTERSECT",VERTEX,{"derivedFrom":[sQuery(id+"F0.wireOp",EDGE,"E11"),subQ0]}),-1.0]])],"derivedFrom":subQ0})])],"isStart":true});}
            var Q52;
            {var subQ0=sQuery(id+"F0.wireOp",EDGE,"E11");Q52=makeQuery(id+"F1.opExtrude","CAP_EDGE",EDGE,{"disambiguationData":[OSD([subQ0]),TDD([makeQuery(id+"F0.imprint","IMPRINT",EDGE,{"disambiguationData":[TD([[makeQuery(id+"F0.imprint","INTERSECT",VERTEX,{"derivedFrom":[subQ0,sQuery(id+"F0.wireOp",EDGE,"E29.trimOffspring")]}),1.0]])],"derivedFrom":subQ0})])],"isStart":true});}
            var Q53;
            {var subQ0=sQuery(id+"F0.wireOp",EDGE,"E29.trimOffspring");Q53=makeQuery(id+"F1.opExtrude","CAP_EDGE",EDGE,{"disambiguationData":[OSD([subQ0]),TDD([makeQuery(id+"F0.imprint","IMPRINT",EDGE,{"disambiguationData":[TD([[makeQuery(id+"F0.imprint","INTERSECT",VERTEX,{"derivedFrom":[sQuery(id+"F0.wireOp",EDGE,"E11"),subQ0]}),-1.0]])],"derivedFrom":subQ0})])],"isStart":true});}
            var Q54;
            {var subQ0=sQuery(id+"F0.wireOp",EDGE,"E11");Q54=makeQuery(id+"F1.opExtrude","CAP_EDGE",EDGE,{"disambiguationData":[OSD([subQ0]),TDD([makeQuery(id+"F0.imprint","IMPRINT",EDGE,{"disambiguationData":[TD([[makeQuery(id+"F0.imprint","INTERSECT",VERTEX,{"derivedFrom":[subQ0,sQuery(id+"F0.wireOp",EDGE,"E25.trimOffspring")]}),-1.0]])],"derivedFrom":subQ0})])],"isStart":true});}
            var Q55;
            Q55=makeQuery(id+"F1.opExtrude","CAP_EDGE",EDGE,{"disambiguationData":[OSD([sQuery(id+"F0.wireOp",EDGE,"E25.trimOffspring")])],"isStart":true});
            var Q56;
            {var subQ0=sQuery(id+"F0.wireOp",EDGE,"E12");Q56=makeQuery(id+"F1.opExtrude","CAP_EDGE",EDGE,{"disambiguationData":[OSD([subQ0]),TDD([makeQuery(id+"F0.imprint","IMPRINT",EDGE,{"disambiguationData":[TD([[makeQuery(id+"F0.imprint","INTERSECT",VERTEX,{"derivedFrom":[subQ0,sQuery(id+"F0.wireOp",EDGE,"E29.trimOffspring")]}),1.0]])],"derivedFrom":subQ0})])],"isStart":true});}
            var Q57;
            {var subQ0=sQuery(id+"F0.wireOp",EDGE,"E30.trimOffspring");Q57=makeQuery(id+"F1.opExtrude","CAP_EDGE",EDGE,{"disambiguationData":[OSD([subQ0]),TDD([makeQuery(id+"F0.imprint","IMPRINT",EDGE,{"disambiguationData":[TD([[makeQuery(id+"F0.imprint","INTERSECT",VERTEX,{"derivedFrom":[sQuery(id+"F0.wireOp",EDGE,"E17.trimOffspring"),subQ0]}),-1.0]])],"derivedFrom":subQ0})])],"isStart":true});}
            var Q58;
            {var subQ0=sQuery(id+"F0.wireOp",EDGE,"E21.trimOffspring");Q58=makeQuery(id+"F1.opExtrude","CAP_EDGE",EDGE,{"disambiguationData":[OSD([subQ0]),TDD([makeQuery(id+"F0.imprint","IMPRINT",EDGE,{"disambiguationData":[TD([[makeQuery(id+"F0.imprint","INTERSECT",VERTEX,{"derivedFrom":[sQuery(id+"F0.wireOp",EDGE,"E20.trimOffspring"),subQ0]}),1.0]])],"derivedFrom":subQ0})])],"isStart":false});}
            var Q59;
            {var subQ0=sQuery(id+"F0.wireOp",EDGE,"E13");Q59=makeQuery(id+"F1.opExtrude","CAP_EDGE",EDGE,{"disambiguationData":[OSD([subQ0]),TDD([makeQuery(id+"F0.imprint","IMPRINT",EDGE,{"disambiguationData":[TD([[makeQuery(id+"F0.imprint","INTERSECT",VERTEX,{"derivedFrom":[subQ0,sQuery(id+"F0.wireOp",EDGE,"E20.trimOffspring")]}),1.0]])],"derivedFrom":subQ0})])],"isStart":false});}
            var Q60;
            {var subQ0=sQuery(id+"F0.wireOp",EDGE,"E20.trimOffspring");Q60=makeQuery(id+"F1.opExtrude","CAP_EDGE",EDGE,{"disambiguationData":[OSD([subQ0]),TDD([makeQuery(id+"F0.imprint","IMPRINT",EDGE,{"disambiguationData":[TD([[makeQuery(id+"F0.imprint","INTERSECT",VERTEX,{"derivedFrom":[sQuery(id+"F0.wireOp",EDGE,"E13"),subQ0]}),-1.0]])],"derivedFrom":subQ0})])],"isStart":false});}
            var Q61;
            {var subQ0=sQuery(id+"F0.wireOp",EDGE,"E19.trimOffspring");Q61=makeQuery(id+"F1.opExtrude","CAP_EDGE",EDGE,{"disambiguationData":[OSD([subQ0]),TDD([makeQuery(id+"F0.imprint","IMPRINT",EDGE,{"disambiguationData":[TD([[makeQuery(id+"F0.imprint","INTERSECT",VERTEX,{"derivedFrom":[subQ0,sQuery(id+"F0.wireOp",EDGE,"E21.trimOffspring")]}),1.0]])],"derivedFrom":subQ0})])],"isStart":false});}
            var Q62;
            {var subQ0=sQuery(id+"F0.wireOp",EDGE,"E12");Q62=makeQuery(id+"F1.opExtrude","CAP_EDGE",EDGE,{"disambiguationData":[OSD([subQ0]),TDD([makeQuery(id+"F0.imprint","IMPRINT",EDGE,{"disambiguationData":[TD([[makeQuery(id+"F0.imprint","INTERSECT",VERTEX,{"derivedFrom":[subQ0,sQuery(id+"F0.wireOp",EDGE,"E29.trimOffspring")]}),1.0]])],"derivedFrom":subQ0})])],"isStart":false});}
            fillet(context, id + "F9", {"entities" : qUnion([Q0, Q1, Q2, Q3, Q4, Q5, Q6, Q7, Q8, Q9, Q10, Q11, Q12, Q13, Q14, Q15, Q16, Q17, Q18, Q19, Q20, Q21, Q22, Q23, Q24, Q25, Q26, Q27, Q28, Q29, Q30, Q31, Q32, Q33, Q34, Q35, Q36, Q37, Q38, Q39, Q40, Q41, Q42, Q43, Q44, Q45, Q46, Q47, Q48, Q49, Q50, Q51, Q52, Q53, Q54, Q55, Q56, Q57, Q58, Q59, Q60, Q61, Q62]), "radius" : 1.2 * mm, "tangentPropagation" : true, "allowEdgeOverflow" : false});
        }
        {
            var Q0;
            Q0=makeQuery(id+"F6.boolean.opBoolean","INTERSECT",EDGE,{"disambiguationData":[OD(1.0)],"derivedFrom":[makeQuery(id+"F1.opExtrude","CAP_FACE",FACE,{"disambiguationData":[OSD([sQuery(id+"F0.wireOp",EDGE,"E4"),sQuery(id+"F0.wireOp",EDGE,"E5"),sQuery(id+"F0.wireOp",EDGE,"E7"),sQuery(id+"F0.wireOp",EDGE,"E8"),sQuery(id+"F0.wireOp",EDGE,"E11"),sQuery(id+"F0.wireOp",EDGE,"E12"),sQuery(id+"F0.wireOp",EDGE,"E13"),sQuery(id+"F0.wireOp",EDGE,"E14"),sQuery(id+"F0.wireOp",EDGE,"E15.trimOffspring"),sQuery(id+"F0.wireOp",EDGE,"E16.trimOffspring"),sQuery(id+"F0.wireOp",EDGE,"E17.trimOffspring"),sQuery(id+"F0.wireOp",EDGE,"E18.trimOffspring"),sQuery(id+"F0.wireOp",EDGE,"E19.trimOffspring"),sQuery(id+"F0.wireOp",EDGE,"E20.trimOffspring"),sQuery(id+"F0.wireOp",EDGE,"E21.trimOffspring"),sQuery(id+"F0.wireOp",EDGE,"E22.trimOffspring"),sQuery(id+"F0.wireOp",EDGE,"E23.trimOffspring"),sQuery(id+"F0.wireOp",EDGE,"E24.trimOffspring"),sQuery(id+"F0.wireOp",EDGE,"E25.trimOffspring"),sQuery(id+"F0.wireOp",EDGE,"E26.trimOffspring"),sQuery(id+"F0.wireOp",EDGE,"E27.trimOffspring"),sQuery(id+"F0.wireOp",EDGE,"E28.trimOffspring"),sQuery(id+"F0.wireOp",EDGE,"E29.trimOffspring"),sQuery(id+"F0.wireOp",EDGE,"E30.trimOffspring")])],"isStart":false}),makeQuery(id+"F6.opRevolve","SWEPT_FACE",FACE,{"disambiguationData":[OSD([sQuery(id+"F5.wireOp",EDGE,"E48.0")])]})]});
            var Q1;
            Q1=makeQuery(id+"F6.boolean.opBoolean","INTERSECT",EDGE,{"disambiguationData":[OD(0.0)],"derivedFrom":[makeQuery(id+"F1.opExtrude","CAP_FACE",FACE,{"disambiguationData":[OSD([sQuery(id+"F0.wireOp",EDGE,"E4"),sQuery(id+"F0.wireOp",EDGE,"E5"),sQuery(id+"F0.wireOp",EDGE,"E7"),sQuery(id+"F0.wireOp",EDGE,"E8"),sQuery(id+"F0.wireOp",EDGE,"E11"),sQuery(id+"F0.wireOp",EDGE,"E12"),sQuery(id+"F0.wireOp",EDGE,"E13"),sQuery(id+"F0.wireOp",EDGE,"E14"),sQuery(id+"F0.wireOp",EDGE,"E15.trimOffspring"),sQuery(id+"F0.wireOp",EDGE,"E16.trimOffspring"),sQuery(id+"F0.wireOp",EDGE,"E17.trimOffspring"),sQuery(id+"F0.wireOp",EDGE,"E18.trimOffspring"),sQuery(id+"F0.wireOp",EDGE,"E19.trimOffspring"),sQuery(id+"F0.wireOp",EDGE,"E20.trimOffspring"),sQuery(id+"F0.wireOp",EDGE,"E21.trimOffspring"),sQuery(id+"F0.wireOp",EDGE,"E22.trimOffspring"),sQuery(id+"F0.wireOp",EDGE,"E23.trimOffspring"),sQuery(id+"F0.wireOp",EDGE,"E24.trimOffspring"),sQuery(id+"F0.wireOp",EDGE,"E25.trimOffspring"),sQuery(id+"F0.wireOp",EDGE,"E26.trimOffspring"),sQuery(id+"F0.wireOp",EDGE,"E27.trimOffspring"),sQuery(id+"F0.wireOp",EDGE,"E28.trimOffspring"),sQuery(id+"F0.wireOp",EDGE,"E29.trimOffspring"),sQuery(id+"F0.wireOp",EDGE,"E30.trimOffspring")])],"isStart":false}),makeQuery(id+"F6.opRevolve","SWEPT_FACE",FACE,{"disambiguationData":[OSD([sQuery(id+"F5.wireOp",EDGE,"E48.0")])]})]});
            var Q2;
            Q2=makeQuery(id+"F6.boolean.opBoolean","INTERSECT",EDGE,{"disambiguationData":[OD(2.0)],"derivedFrom":[makeQuery(id+"F1.opExtrude","CAP_FACE",FACE,{"disambiguationData":[OSD([sQuery(id+"F0.wireOp",EDGE,"E4"),sQuery(id+"F0.wireOp",EDGE,"E5"),sQuery(id+"F0.wireOp",EDGE,"E7"),sQuery(id+"F0.wireOp",EDGE,"E8"),sQuery(id+"F0.wireOp",EDGE,"E11"),sQuery(id+"F0.wireOp",EDGE,"E12"),sQuery(id+"F0.wireOp",EDGE,"E13"),sQuery(id+"F0.wireOp",EDGE,"E14"),sQuery(id+"F0.wireOp",EDGE,"E15.trimOffspring"),sQuery(id+"F0.wireOp",EDGE,"E16.trimOffspring"),sQuery(id+"F0.wireOp",EDGE,"E17.trimOffspring"),sQuery(id+"F0.wireOp",EDGE,"E18.trimOffspring"),sQuery(id+"F0.wireOp",EDGE,"E19.trimOffspring"),sQuery(id+"F0.wireOp",EDGE,"E20.trimOffspring"),sQuery(id+"F0.wireOp",EDGE,"E21.trimOffspring"),sQuery(id+"F0.wireOp",EDGE,"E22.trimOffspring"),sQuery(id+"F0.wireOp",EDGE,"E23.trimOffspring"),sQuery(id+"F0.wireOp",EDGE,"E24.trimOffspring"),sQuery(id+"F0.wireOp",EDGE,"E25.trimOffspring"),sQuery(id+"F0.wireOp",EDGE,"E26.trimOffspring"),sQuery(id+"F0.wireOp",EDGE,"E27.trimOffspring"),sQuery(id+"F0.wireOp",EDGE,"E28.trimOffspring"),sQuery(id+"F0.wireOp",EDGE,"E29.trimOffspring"),sQuery(id+"F0.wireOp",EDGE,"E30.trimOffspring")])],"isStart":false}),makeQuery(id+"F6.opRevolve","SWEPT_FACE",FACE,{"disambiguationData":[OSD([sQuery(id+"F5.wireOp",EDGE,"E48.0")])]})]});
            var Q3;
            Q3=makeQuery(id+"F7.boolean.opBoolean","INTERSECT",EDGE,{"disambiguationData":[OD(2.0)],"derivedFrom":[makeQuery(id+"F1.opExtrude","CAP_FACE",FACE,{"disambiguationData":[OSD([sQuery(id+"F0.wireOp",EDGE,"E4"),sQuery(id+"F0.wireOp",EDGE,"E5"),sQuery(id+"F0.wireOp",EDGE,"E7"),sQuery(id+"F0.wireOp",EDGE,"E8"),sQuery(id+"F0.wireOp",EDGE,"E11"),sQuery(id+"F0.wireOp",EDGE,"E12"),sQuery(id+"F0.wireOp",EDGE,"E13"),sQuery(id+"F0.wireOp",EDGE,"E14"),sQuery(id+"F0.wireOp",EDGE,"E15.trimOffspring"),sQuery(id+"F0.wireOp",EDGE,"E16.trimOffspring"),sQuery(id+"F0.wireOp",EDGE,"E17.trimOffspring"),sQuery(id+"F0.wireOp",EDGE,"E18.trimOffspring"),sQuery(id+"F0.wireOp",EDGE,"E19.trimOffspring"),sQuery(id+"F0.wireOp",EDGE,"E20.trimOffspring"),sQuery(id+"F0.wireOp",EDGE,"E21.trimOffspring"),sQuery(id+"F0.wireOp",EDGE,"E22.trimOffspring"),sQuery(id+"F0.wireOp",EDGE,"E23.trimOffspring"),sQuery(id+"F0.wireOp",EDGE,"E24.trimOffspring"),sQuery(id+"F0.wireOp",EDGE,"E25.trimOffspring"),sQuery(id+"F0.wireOp",EDGE,"E26.trimOffspring"),sQuery(id+"F0.wireOp",EDGE,"E27.trimOffspring"),sQuery(id+"F0.wireOp",EDGE,"E28.trimOffspring"),sQuery(id+"F0.wireOp",EDGE,"E29.trimOffspring"),sQuery(id+"F0.wireOp",EDGE,"E30.trimOffspring")])],"isStart":false}),makeQuery(id+"F7.opRevolve","SWEPT_FACE",FACE,{"disambiguationData":[OSD([sQuery(id+"F5.wireOp",EDGE,"E52.0")])]})]});
            var Q4;
            Q4=makeQuery(id+"F7.boolean.opBoolean","INTERSECT",EDGE,{"disambiguationData":[OD(1.0)],"derivedFrom":[makeQuery(id+"F1.opExtrude","CAP_FACE",FACE,{"disambiguationData":[OSD([sQuery(id+"F0.wireOp",EDGE,"E4"),sQuery(id+"F0.wireOp",EDGE,"E5"),sQuery(id+"F0.wireOp",EDGE,"E7"),sQuery(id+"F0.wireOp",EDGE,"E8"),sQuery(id+"F0.wireOp",EDGE,"E11"),sQuery(id+"F0.wireOp",EDGE,"E12"),sQuery(id+"F0.wireOp",EDGE,"E13"),sQuery(id+"F0.wireOp",EDGE,"E14"),sQuery(id+"F0.wireOp",EDGE,"E15.trimOffspring"),sQuery(id+"F0.wireOp",EDGE,"E16.trimOffspring"),sQuery(id+"F0.wireOp",EDGE,"E17.trimOffspring"),sQuery(id+"F0.wireOp",EDGE,"E18.trimOffspring"),sQuery(id+"F0.wireOp",EDGE,"E19.trimOffspring"),sQuery(id+"F0.wireOp",EDGE,"E20.trimOffspring"),sQuery(id+"F0.wireOp",EDGE,"E21.trimOffspring"),sQuery(id+"F0.wireOp",EDGE,"E22.trimOffspring"),sQuery(id+"F0.wireOp",EDGE,"E23.trimOffspring"),sQuery(id+"F0.wireOp",EDGE,"E24.trimOffspring"),sQuery(id+"F0.wireOp",EDGE,"E25.trimOffspring"),sQuery(id+"F0.wireOp",EDGE,"E26.trimOffspring"),sQuery(id+"F0.wireOp",EDGE,"E27.trimOffspring"),sQuery(id+"F0.wireOp",EDGE,"E28.trimOffspring"),sQuery(id+"F0.wireOp",EDGE,"E29.trimOffspring"),sQuery(id+"F0.wireOp",EDGE,"E30.trimOffspring")])],"isStart":false}),makeQuery(id+"F7.opRevolve","SWEPT_FACE",FACE,{"disambiguationData":[OSD([sQuery(id+"F5.wireOp",EDGE,"E52.0")])]})]});
            var Q5;
            Q5=makeQuery(id+"F7.boolean.opBoolean","INTERSECT",EDGE,{"disambiguationData":[OD(0.0)],"derivedFrom":[makeQuery(id+"F1.opExtrude","CAP_FACE",FACE,{"disambiguationData":[OSD([sQuery(id+"F0.wireOp",EDGE,"E4"),sQuery(id+"F0.wireOp",EDGE,"E5"),sQuery(id+"F0.wireOp",EDGE,"E7"),sQuery(id+"F0.wireOp",EDGE,"E8"),sQuery(id+"F0.wireOp",EDGE,"E11"),sQuery(id+"F0.wireOp",EDGE,"E12"),sQuery(id+"F0.wireOp",EDGE,"E13"),sQuery(id+"F0.wireOp",EDGE,"E14"),sQuery(id+"F0.wireOp",EDGE,"E15.trimOffspring"),sQuery(id+"F0.wireOp",EDGE,"E16.trimOffspring"),sQuery(id+"F0.wireOp",EDGE,"E17.trimOffspring"),sQuery(id+"F0.wireOp",EDGE,"E18.trimOffspring"),sQuery(id+"F0.wireOp",EDGE,"E19.trimOffspring"),sQuery(id+"F0.wireOp",EDGE,"E20.trimOffspring"),sQuery(id+"F0.wireOp",EDGE,"E21.trimOffspring"),sQuery(id+"F0.wireOp",EDGE,"E22.trimOffspring"),sQuery(id+"F0.wireOp",EDGE,"E23.trimOffspring"),sQuery(id+"F0.wireOp",EDGE,"E24.trimOffspring"),sQuery(id+"F0.wireOp",EDGE,"E25.trimOffspring"),sQuery(id+"F0.wireOp",EDGE,"E26.trimOffspring"),sQuery(id+"F0.wireOp",EDGE,"E27.trimOffspring"),sQuery(id+"F0.wireOp",EDGE,"E28.trimOffspring"),sQuery(id+"F0.wireOp",EDGE,"E29.trimOffspring"),sQuery(id+"F0.wireOp",EDGE,"E30.trimOffspring")])],"isStart":false}),makeQuery(id+"F7.opRevolve","SWEPT_FACE",FACE,{"disambiguationData":[OSD([sQuery(id+"F5.wireOp",EDGE,"E52.0")])]})]});
            var Q6;
            Q6=makeQuery(id+"F8.boolean.opBoolean","INTERSECT",EDGE,{"disambiguationData":[OD(1.0)],"derivedFrom":[makeQuery(id+"F1.opExtrude","CAP_FACE",FACE,{"disambiguationData":[OSD([sQuery(id+"F0.wireOp",EDGE,"E4"),sQuery(id+"F0.wireOp",EDGE,"E5"),sQuery(id+"F0.wireOp",EDGE,"E7"),sQuery(id+"F0.wireOp",EDGE,"E8"),sQuery(id+"F0.wireOp",EDGE,"E11"),sQuery(id+"F0.wireOp",EDGE,"E12"),sQuery(id+"F0.wireOp",EDGE,"E13"),sQuery(id+"F0.wireOp",EDGE,"E14"),sQuery(id+"F0.wireOp",EDGE,"E15.trimOffspring"),sQuery(id+"F0.wireOp",EDGE,"E16.trimOffspring"),sQuery(id+"F0.wireOp",EDGE,"E17.trimOffspring"),sQuery(id+"F0.wireOp",EDGE,"E18.trimOffspring"),sQuery(id+"F0.wireOp",EDGE,"E19.trimOffspring"),sQuery(id+"F0.wireOp",EDGE,"E20.trimOffspring"),sQuery(id+"F0.wireOp",EDGE,"E21.trimOffspring"),sQuery(id+"F0.wireOp",EDGE,"E22.trimOffspring"),sQuery(id+"F0.wireOp",EDGE,"E23.trimOffspring"),sQuery(id+"F0.wireOp",EDGE,"E24.trimOffspring"),sQuery(id+"F0.wireOp",EDGE,"E25.trimOffspring"),sQuery(id+"F0.wireOp",EDGE,"E26.trimOffspring"),sQuery(id+"F0.wireOp",EDGE,"E27.trimOffspring"),sQuery(id+"F0.wireOp",EDGE,"E28.trimOffspring"),sQuery(id+"F0.wireOp",EDGE,"E29.trimOffspring"),sQuery(id+"F0.wireOp",EDGE,"E30.trimOffspring")])],"isStart":false}),makeQuery(id+"F8.opRevolve","SWEPT_FACE",FACE,{"disambiguationData":[OSD([sQuery(id+"F5.wireOp",EDGE,"E50.0")])]})]});
            var Q7;
            Q7=makeQuery(id+"F8.boolean.opBoolean","INTERSECT",EDGE,{"disambiguationData":[OD(2.0)],"derivedFrom":[makeQuery(id+"F1.opExtrude","CAP_FACE",FACE,{"disambiguationData":[OSD([sQuery(id+"F0.wireOp",EDGE,"E4"),sQuery(id+"F0.wireOp",EDGE,"E5"),sQuery(id+"F0.wireOp",EDGE,"E7"),sQuery(id+"F0.wireOp",EDGE,"E8"),sQuery(id+"F0.wireOp",EDGE,"E11"),sQuery(id+"F0.wireOp",EDGE,"E12"),sQuery(id+"F0.wireOp",EDGE,"E13"),sQuery(id+"F0.wireOp",EDGE,"E14"),sQuery(id+"F0.wireOp",EDGE,"E15.trimOffspring"),sQuery(id+"F0.wireOp",EDGE,"E16.trimOffspring"),sQuery(id+"F0.wireOp",EDGE,"E17.trimOffspring"),sQuery(id+"F0.wireOp",EDGE,"E18.trimOffspring"),sQuery(id+"F0.wireOp",EDGE,"E19.trimOffspring"),sQuery(id+"F0.wireOp",EDGE,"E20.trimOffspring"),sQuery(id+"F0.wireOp",EDGE,"E21.trimOffspring"),sQuery(id+"F0.wireOp",EDGE,"E22.trimOffspring"),sQuery(id+"F0.wireOp",EDGE,"E23.trimOffspring"),sQuery(id+"F0.wireOp",EDGE,"E24.trimOffspring"),sQuery(id+"F0.wireOp",EDGE,"E25.trimOffspring"),sQuery(id+"F0.wireOp",EDGE,"E26.trimOffspring"),sQuery(id+"F0.wireOp",EDGE,"E27.trimOffspring"),sQuery(id+"F0.wireOp",EDGE,"E28.trimOffspring"),sQuery(id+"F0.wireOp",EDGE,"E29.trimOffspring"),sQuery(id+"F0.wireOp",EDGE,"E30.trimOffspring")])],"isStart":false}),makeQuery(id+"F8.opRevolve","SWEPT_FACE",FACE,{"disambiguationData":[OSD([sQuery(id+"F5.wireOp",EDGE,"E50.0")])]})]});
            var Q8;
            Q8=makeQuery(id+"F8.boolean.opBoolean","INTERSECT",EDGE,{"disambiguationData":[OD(0.0)],"derivedFrom":[makeQuery(id+"F1.opExtrude","CAP_FACE",FACE,{"disambiguationData":[OSD([sQuery(id+"F0.wireOp",EDGE,"E4"),sQuery(id+"F0.wireOp",EDGE,"E5"),sQuery(id+"F0.wireOp",EDGE,"E7"),sQuery(id+"F0.wireOp",EDGE,"E8"),sQuery(id+"F0.wireOp",EDGE,"E11"),sQuery(id+"F0.wireOp",EDGE,"E12"),sQuery(id+"F0.wireOp",EDGE,"E13"),sQuery(id+"F0.wireOp",EDGE,"E14"),sQuery(id+"F0.wireOp",EDGE,"E15.trimOffspring"),sQuery(id+"F0.wireOp",EDGE,"E16.trimOffspring"),sQuery(id+"F0.wireOp",EDGE,"E17.trimOffspring"),sQuery(id+"F0.wireOp",EDGE,"E18.trimOffspring"),sQuery(id+"F0.wireOp",EDGE,"E19.trimOffspring"),sQuery(id+"F0.wireOp",EDGE,"E20.trimOffspring"),sQuery(id+"F0.wireOp",EDGE,"E21.trimOffspring"),sQuery(id+"F0.wireOp",EDGE,"E22.trimOffspring"),sQuery(id+"F0.wireOp",EDGE,"E23.trimOffspring"),sQuery(id+"F0.wireOp",EDGE,"E24.trimOffspring"),sQuery(id+"F0.wireOp",EDGE,"E25.trimOffspring"),sQuery(id+"F0.wireOp",EDGE,"E26.trimOffspring"),sQuery(id+"F0.wireOp",EDGE,"E27.trimOffspring"),sQuery(id+"F0.wireOp",EDGE,"E28.trimOffspring"),sQuery(id+"F0.wireOp",EDGE,"E29.trimOffspring"),sQuery(id+"F0.wireOp",EDGE,"E30.trimOffspring")])],"isStart":false}),makeQuery(id+"F8.opRevolve","SWEPT_FACE",FACE,{"disambiguationData":[OSD([sQuery(id+"F5.wireOp",EDGE,"E50.0")])]})]});
            fillet(context, id + "F10", {"entities" : qUnion([Q0, Q1, Q2, Q3, Q4, Q5, Q6, Q7, Q8]), "radius" : 1 * mm, "tangentPropagation" : true, "allowEdgeOverflow" : false});
        }
    });
